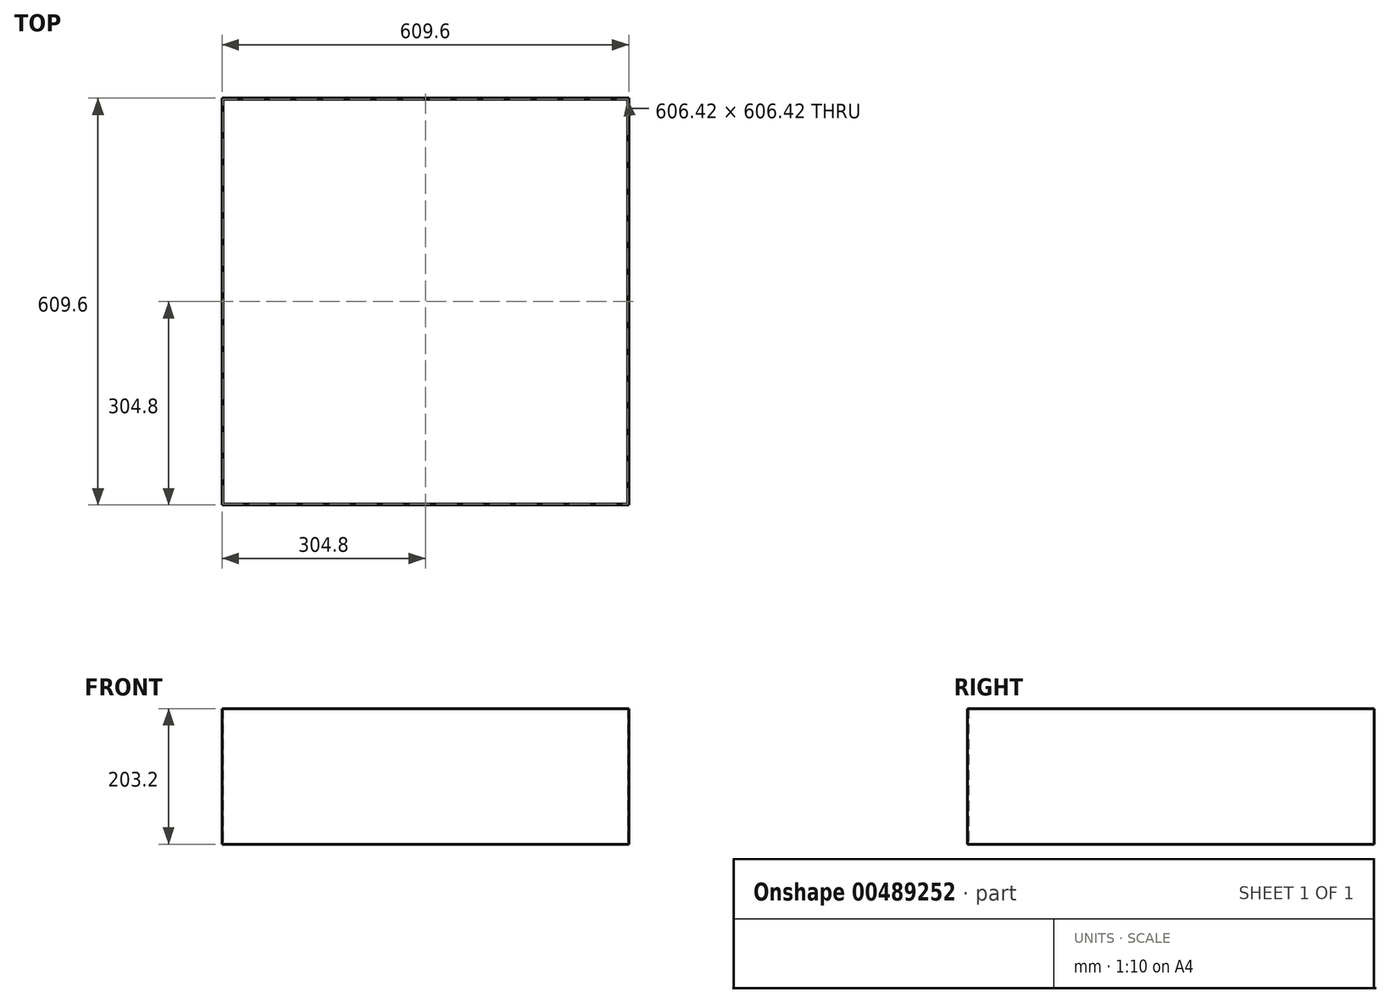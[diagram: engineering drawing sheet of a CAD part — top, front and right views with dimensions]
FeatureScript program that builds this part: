
annotation { "Feature Type Name" : "Feature", "Feature Type Description" : "" }
export const myFeature = defineFeature(function(context is Context, id is Id, definition is map)
    precondition{}
    {
        {
            var Q0;
            Q0=qCreatedBy(makeId("Top.planeOp"),FACE);
            var sketch = newSketch(context, id + "F0", { "sketchPlane" : qUnion([Q0])});
            skLineSegment(sketch, "E0.bottom", {"start": v(304.8, 304.8) * mm, "end": v(-304.8, 304.8) * mm});
            skLineSegment(sketch, "E0.top", {"start": v(304.8, -304.8) * mm, "end": v(-304.8, -304.8) * mm});
            skLineSegment(sketch, "E0.left", {"start": v(304.8, 304.8) * mm, "end": v(304.8, -304.8) * mm});
            skLineSegment(sketch, "E0.right", {"start": v(-304.8, 304.8) * mm, "end": v(-304.8, -304.8) * mm});
            skPoint(sketch, "E0.middle", {"position": v(0, 0) * mm});
            skSolve(sketch);
        }
        {
            var Q0;
            Q0=makeQuery(id+"F0.imprint","IMPRINT",FACE,{"disambiguationData":[TD([[makeQuery(id+"F0.imprint","IMPRINT",EDGE,{"derivedFrom":sQuery(id+"F0.wireOp",EDGE,"E0.bottom")}),1.0]])]});
            extrude(context, id + "F1", {"entities" : qUnion([Q0]), "depth" : 203.2 * mm, "offsetDistance" : 25.4 * mm});
        }
        {
            var Q0;
            Q0=makeQuery(id+"F1.opExtrude","CAP_FACE",FACE,{"disambiguationData":[OSD([sQuery(id+"F0.wireOp",EDGE,"E0.bottom"),sQuery(id+"F0.wireOp",EDGE,"E0.top"),sQuery(id+"F0.wireOp",EDGE,"E0.left"),sQuery(id+"F0.wireOp",EDGE,"E0.right")])],"isStart":false});
            var Q1;
            Q1=makeQuery(id+"F1.opExtrude","CAP_FACE",FACE,{"disambiguationData":[OSD([sQuery(id+"F0.wireOp",EDGE,"E0.bottom"),sQuery(id+"F0.wireOp",EDGE,"E0.top"),sQuery(id+"F0.wireOp",EDGE,"E0.left"),sQuery(id+"F0.wireOp",EDGE,"E0.right")])],"isStart":true});
            shell(context, id + "F2", {"entities" : qUnion([Q0, Q1]), "thickness" : 1.59 * mm});
        }
    });
